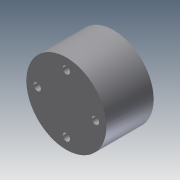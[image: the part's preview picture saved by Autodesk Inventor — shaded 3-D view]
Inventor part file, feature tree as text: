
AUTODESK INVENTOR PART (.ipt)
format: ipt  version: 2011 (Build 150239000, 239)  size: 97,280 bytes
history: native  units: in
note: dims shown in document units (in); Inventor stores cm internally (conversion verified against a paired STEP export)
features: extrude x3, sketch x3
ambient origin geometry x8: Origin, YZ Plane, XZ Plane, XY Plane, X Axis, Y Axis, Z Axis, Center Point
bodies: Solid1 (feature_tree)
feature tree (6):
  extrude  "Extrusion1"  Depth=0.3937in TaperAngle=0.0deg
  extrude  "Extrusion2"  Depth=0.0787in
  extrude  "Extrusion3"  Depth=0.0787in
  sketch  "Sketch1"  dims[d0=0.8661in d1=0.3937in d2=0.0in]
  sketch  "Sketch2"  dims[d3=0.6299in d4=0.0787in]
  sketch  "Sketch3"  dims[d5=0.0787in d6=0.0787in d7=0.0787in d8=0.3937in d9=0.0in d10=0.1181in d11=0.0in]
